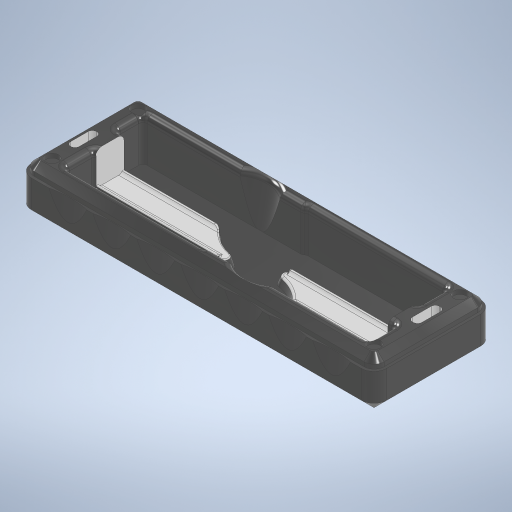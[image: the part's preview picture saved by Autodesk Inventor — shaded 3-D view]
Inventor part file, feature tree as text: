
AUTODESK INVENTOR PART (.ipt)
format: ipt  version: 2024.1 (Build 281209000, 209)  size: 944,128 bytes
history: native  units: mm
features: fillet x8, other x4, extrude x4, sketch x4
ambient origin geometry x8: Origin, YZ Plane, XZ Plane, XY Plane, X Axis, Y Axis, Z Axis, Center Point
bodies: Body1 (feature_tree)
feature tree (20):
  other  "pen-case.ipt"
  extrude  "Extrusion1"  Depth=10.0mm
  extrude  "Extrusion2"  Depth=0.5mm
  fillet  "Fillet1"  Radius=12.8mm
  fillet  "Fillet2"  Radius=0.4mm
  extrude  "Extrusion3"  Depth=15.8mm TaperAngle=0.0deg
  fillet  "Fillet5"  Radius=0.55mm
  fillet  "Fillet6"  Radius=0.55mm
  fillet  "Fillet7"  Radius=0.55mm
  extrude  "Extrusion4"  Depth=2.0mm
  fillet  "Fillet8"  Radius=0.5mm
  fillet  "Fillet3"  Radius=14.0mm
  fillet  "Fillet4"  Radius=2.0mm
  other  "case::pen-case.ipt"
  other  "TaggingFeature1"
  sketch  "Sketch1"  dims[d0=10.0mm d1=138.0mm]
  sketch  "Sketch2"  dims[d2=0.5mm d3=0.5mm d4=12.8mm d5=0.4mm]
  sketch  "Sketch3"  dims[d6=0.4mm d7=15.8mm d8=0.0mm d9=0.55mm d10=0.55mm d11=0.55mm]
  sketch  "Sketch4"  dims[d12=2.0mm d13=0.0mm d14=2.0mm d15=0.5mm d16=14.0mm d17=0.0mm d18=2.0mm d19=2.0mm d20=0.5mm d21=1.0mm d22=0.5mm d23=14.0mm d24=0.0mm d25=2.0mm]
  other  "case"
